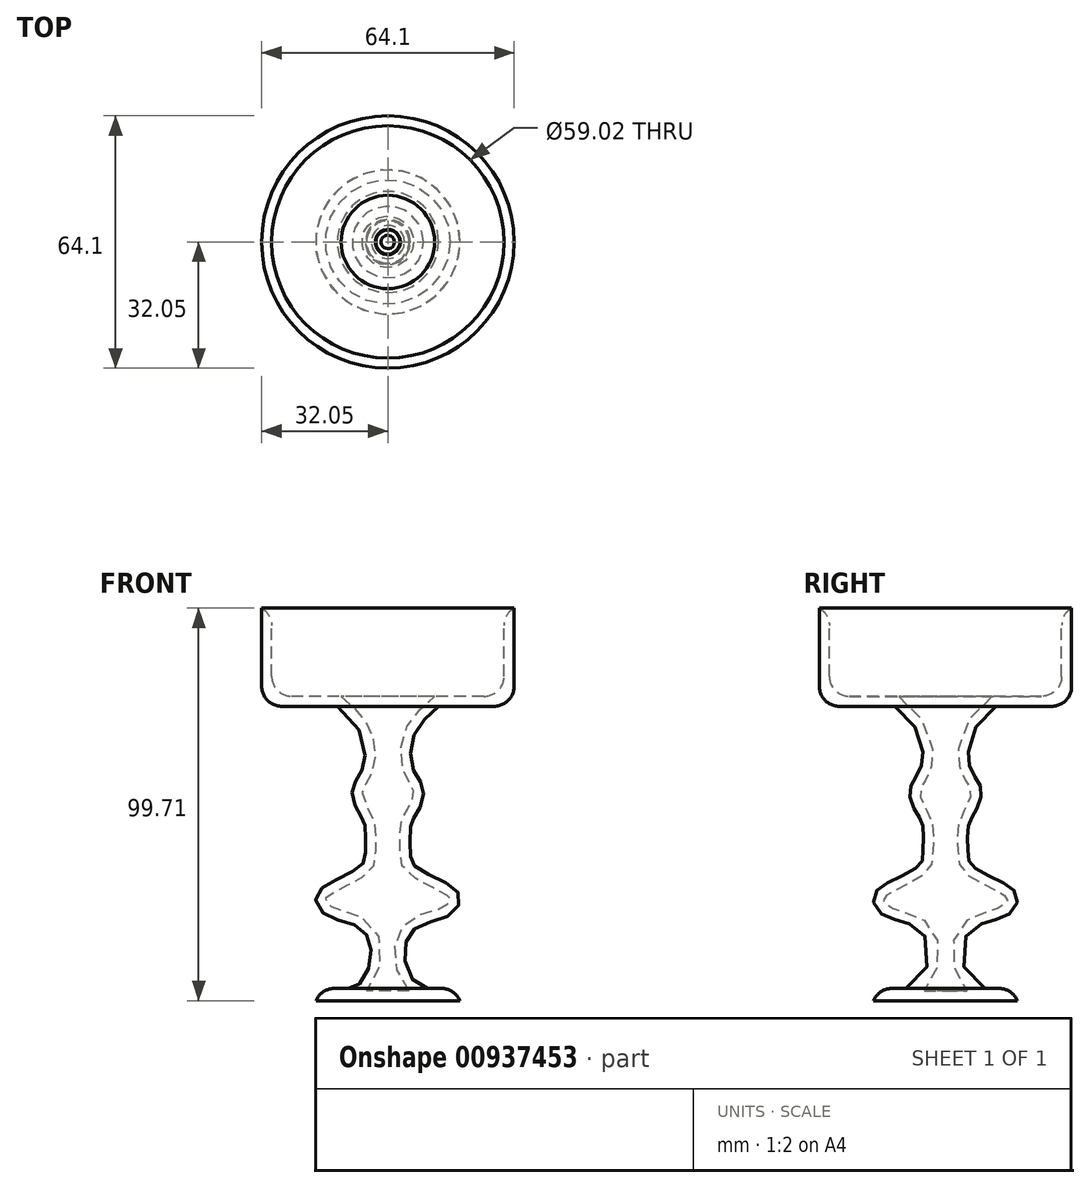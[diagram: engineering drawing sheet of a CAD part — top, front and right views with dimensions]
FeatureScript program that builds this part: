
annotation { "Feature Type Name" : "Feature", "Feature Type Description" : "" }
export const myFeature = defineFeature(function(context is Context, id is Id, definition is map)
    precondition{}
    {
        {
            var Q0;
            Q0=qCreatedBy(makeId("Front.planeOp"),FACE);
            var sketch = newSketch(context, id + "F0", { "sketchPlane" : qUnion([Q0])});
            skLineSegment(sketch, "E0", {"start": v(0, 30.98) * mm, "end": v(0, -43.8) * mm});
            skLineSegment(sketch, "E1", {"start": v(0, -43.8) * mm, "end": v(18.28, -43.8) * mm});
            skLineSegment(sketch, "E2", {"start": v(18.28, -43.8) * mm, "end": v(18.28, -39.77) * mm});
            skPoint(sketch, "E3.8.internal.snap0", {"position": v(0, -6.41) * mm});
            skFitSpline(sketch, "E3", {"points": [v(18.28, -39.77) * mm, v(7.6, -39.77) * mm, v(4.27, -30.75) * mm, v(7.83, -24.81) * mm, v(15.9, -21.96) * mm, v(18.28, -17.21) * mm, v(13.3, -13.18) * mm, v(6.41, -9.14) * mm, v(5.7, -6.41) * mm, v(5.7, 0) * mm, v(6.41, 2.26) * mm, v(8.55, 6.3) * mm, v(8.78, 10.8) * mm, v(6.41, 15.08) * mm, v(6.65, 23.62) * mm, v(12.82, 30.98) * mm], "startDerivative": vector(-140.64, -31.07) * mm, "endDerivative": vector(90.96, 80.77) * mm});
            skLineSegment(sketch, "E4", {"start": v(12.82, 30.98) * mm, "end": v(32.05, 30.98) * mm});
            skLineSegment(sketch, "E5", {"start": v(32.05, 30.98) * mm, "end": v(32.05, 55.91) * mm});
            skLineSegment(sketch, "E6", {"start": v(32.05, 55.91) * mm, "end": v(0, 55.91) * mm});
            skLineSegment(sketch, "E7", {"start": v(0, 55.91) * mm, "end": v(0, 30.98) * mm});
            skSolve(sketch);
        }
        {
            var Q0;
            Q0=makeQuery(id+"F0.imprint","IMPRINT",FACE,{"disambiguationData":[TD([[makeQuery(id+"F0.imprint","IMPRINT",EDGE,{"derivedFrom":sQuery(id+"F0.wireOp",EDGE,"E0")}),1.0]])]});
            var Q1;
            Q1=sQuery(id+"F0.wireOp",EDGE,"E0");
            revolve(context, id + "F1", {"surfaceOperationType" : NewSurfaceOperationType.NEW, "entities" : qUnion([Q0]), "axis" : qUnion([Q1]), "revolveType" : RevolveType.FULL});
        }
        {
            var Q0;
            Q0=makeQuery(id+"F1.opRevolve","SWEPT_FACE",FACE,{"disambiguationData":[OSD([sQuery(id+"F0.wireOp",EDGE,"E6")])]});
            shell(context, id + "F2", {"entities" : qUnion([Q0]), "thickness" : 2.54 * mm});
        }
        {
            var Q0;
            Q0=makeQuery(id+"F1.opRevolve","SWEPT_EDGE",EDGE,{"disambiguationData":[OSD([sQuery(id+"F0.wireOp",EDGE,"E4"),sQuery(id+"F0.wireOp",EDGE,"E5")])]});
            var Q1;
            Q1=makeQuery(id+"F1.opRevolve","SWEPT_EDGE",EDGE,{"disambiguationData":[OSD([sQuery(id+"F0.wireOp",EDGE,"E2"),sQuery(id+"F0.wireOp",EDGE,"E3")])]});
            var Q2;
            Q2=makeQuery(id+"F2.opShell","OFFSET_EDGE",EDGE,{"disambiguationData":[OSD([sQuery(id+"F0.wireOp",EDGE,"E5"),sQuery(id+"F0.wireOp",EDGE,"E6")])]});
            var Q3;
            Q3=makeQuery(id+"F2.opShell","OFFSET_EDGE",EDGE,{"disambiguationData":[OSD([sQuery(id+"F0.wireOp",EDGE,"E4"),sQuery(id+"F0.wireOp",EDGE,"E5")])]});
            fillet(context, id + "F3", {"entities" : qUnion([Q0, Q1, Q2, Q3]), "radius" : 5.08 * mm, "tangentPropagation" : true, "allowEdgeOverflow" : false});
        }
    });
